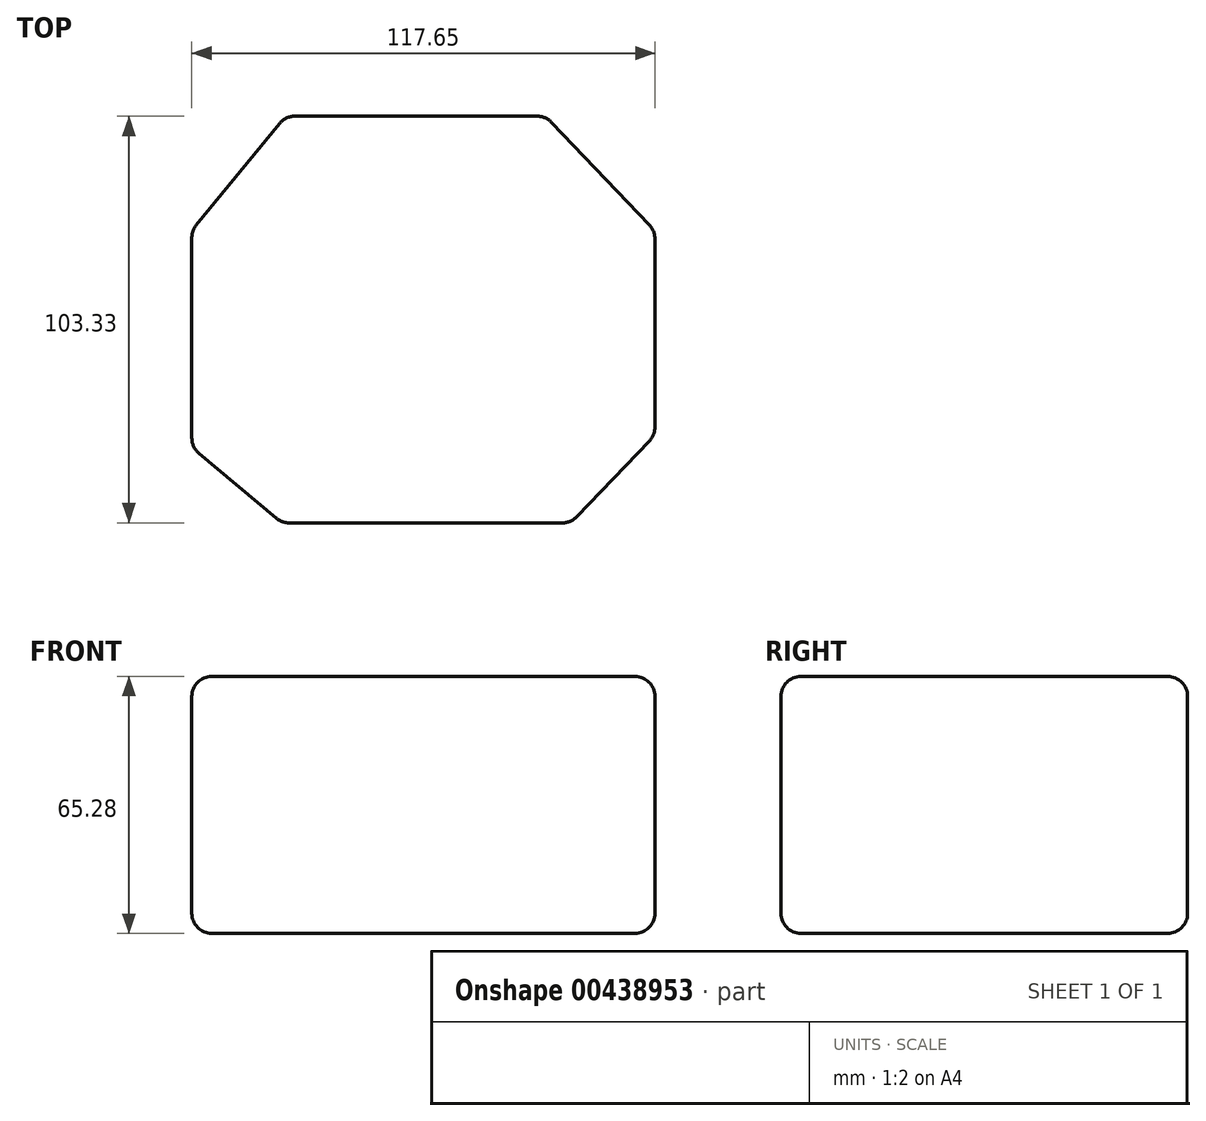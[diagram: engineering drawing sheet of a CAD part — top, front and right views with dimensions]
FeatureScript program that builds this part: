
annotation { "Feature Type Name" : "Feature", "Feature Type Description" : "" }
export const myFeature = defineFeature(function(context is Context, id is Id, definition is map)
    precondition{}
    {
        {
            var Q0;
            Q0=qCreatedBy(makeId("Top.planeOp"),FACE);
            var sketch = newSketch(context, id + "F0", { "sketchPlane" : qUnion([Q0])});
            skLineSegment(sketch, "E0", {"start": v(-32.92, 29.1) * mm, "end": v(33.22, 29.1) * mm});
            skLineSegment(sketch, "E1", {"start": v(33.22, 29.1) * mm, "end": v(60.96, 0) * mm});
            skLineSegment(sketch, "E2", {"start": v(60.96, 0) * mm, "end": v(60.96, -51.97) * mm});
            skLineSegment(sketch, "E3", {"start": v(60.96, -51.97) * mm, "end": v(39.62, -74.22) * mm});
            skLineSegment(sketch, "E4", {"start": v(39.62, -74.22) * mm, "end": v(-33.83, -74.22) * mm});
            skLineSegment(sketch, "E5", {"start": v(-33.83, -74.22) * mm, "end": v(-56.7, -55.02) * mm});
            skLineSegment(sketch, "E6", {"start": v(-56.7, -55.02) * mm, "end": v(-56.7, 0) * mm});
            skLineSegment(sketch, "E7", {"start": v(-56.7, 0) * mm, "end": v(-32.92, 29.1) * mm});
            skSolve(sketch);
        }
        {
            var Q0;
            Q0 = qSketchRegion(id + "F0", true);
            extrude(context, id + "F1", {"entities" : qUnion([Q0]), "depth" : 65.28 * mm});
        }
        {
            var Q0;
            Q0=makeQuery(id+"F1.opExtrude","SWEPT_FACE",FACE,{"disambiguationData":[OSD([sQuery(id+"F0.wireOp",EDGE,"E0")])]});
            var Q1;
            Q1=makeQuery(id+"F1.opExtrude","SWEPT_FACE",FACE,{"disambiguationData":[OSD([sQuery(id+"F0.wireOp",EDGE,"E1")])]});
            var Q2;
            Q2=makeQuery(id+"F1.opExtrude","SWEPT_FACE",FACE,{"disambiguationData":[OSD([sQuery(id+"F0.wireOp",EDGE,"E7")])]});
            var Q3;
            Q3=makeQuery(id+"F1.opExtrude","SWEPT_FACE",FACE,{"disambiguationData":[OSD([sQuery(id+"F0.wireOp",EDGE,"E6")])]});
            var Q4;
            Q4=makeQuery(id+"F1.opExtrude","SWEPT_FACE",FACE,{"disambiguationData":[OSD([sQuery(id+"F0.wireOp",EDGE,"E5")])]});
            var Q5;
            Q5=makeQuery(id+"F1.opExtrude","SWEPT_FACE",FACE,{"disambiguationData":[OSD([sQuery(id+"F0.wireOp",EDGE,"E4")])]});
            var Q6;
            Q6=makeQuery(id+"F1.opExtrude","SWEPT_FACE",FACE,{"disambiguationData":[OSD([sQuery(id+"F0.wireOp",EDGE,"E3")])]});
            var Q7;
            Q7=makeQuery(id+"F1.opExtrude","SWEPT_FACE",FACE,{"disambiguationData":[OSD([sQuery(id+"F0.wireOp",EDGE,"E2")])]});
            var Q8;
            Q8=makeQuery(id+"F1.opExtrude","CAP_EDGE",EDGE,{"disambiguationData":[OSD([sQuery(id+"F0.wireOp",EDGE,"E7")])],"isStart":false});
            var Q9;
            Q9=makeQuery(id+"F1.opExtrude","CAP_EDGE",EDGE,{"disambiguationData":[OSD([sQuery(id+"F0.wireOp",EDGE,"E3")])],"isStart":false});
            var Q10;
            Q10=makeQuery(id+"F1.opExtrude","CAP_EDGE",EDGE,{"disambiguationData":[OSD([sQuery(id+"F0.wireOp",EDGE,"E5")])],"isStart":false});
            var Q11;
            Q11=makeQuery(id+"F1.opExtrude","CAP_EDGE",EDGE,{"disambiguationData":[OSD([sQuery(id+"F0.wireOp",EDGE,"E5")])],"isStart":true});
            var Q12;
            Q12=makeQuery(id+"F1.opExtrude","CAP_EDGE",EDGE,{"disambiguationData":[OSD([sQuery(id+"F0.wireOp",EDGE,"E1")])],"isStart":false});
            var Q13;
            Q13=makeQuery(id+"F1.opExtrude","CAP_EDGE",EDGE,{"disambiguationData":[OSD([sQuery(id+"F0.wireOp",EDGE,"E7")])],"isStart":true});
            var Q14;
            Q14=makeQuery(id+"F1.opExtrude","CAP_EDGE",EDGE,{"disambiguationData":[OSD([sQuery(id+"F0.wireOp",EDGE,"E3")])],"isStart":true});
            var Q15;
            Q15=makeQuery(id+"F1.opExtrude","CAP_EDGE",EDGE,{"disambiguationData":[OSD([sQuery(id+"F0.wireOp",EDGE,"E6")])],"isStart":false});
            var Q16;
            Q16=makeQuery(id+"F1.opExtrude","CAP_EDGE",EDGE,{"disambiguationData":[OSD([sQuery(id+"F0.wireOp",EDGE,"E6")])],"isStart":true});
            var Q17;
            Q17=makeQuery(id+"F1.opExtrude","SWEPT_EDGE",EDGE,{"disambiguationData":[OSD([sQuery(id+"F0.wireOp",EDGE,"E5"),sQuery(id+"F0.wireOp",EDGE,"E6")])]});
            var Q18;
            Q18=makeQuery(id+"F1.opExtrude","CAP_EDGE",EDGE,{"disambiguationData":[OSD([sQuery(id+"F0.wireOp",EDGE,"E0")])],"isStart":false});
            var Q19;
            Q19=makeQuery(id+"F1.opExtrude","SWEPT_EDGE",EDGE,{"disambiguationData":[OSD([sQuery(id+"F0.wireOp",EDGE,"E6"),sQuery(id+"F0.wireOp",EDGE,"E7")])]});
            var Q20;
            Q20=makeQuery(id+"F1.opExtrude","SWEPT_EDGE",EDGE,{"disambiguationData":[OSD([sQuery(id+"F0.wireOp",EDGE,"E0"),sQuery(id+"F0.wireOp",EDGE,"E1")])]});
            var Q21;
            Q21=makeQuery(id+"F1.opExtrude","SWEPT_EDGE",EDGE,{"disambiguationData":[OSD([sQuery(id+"F0.wireOp",EDGE,"E0"),sQuery(id+"F0.wireOp",EDGE,"E7")])]});
            var Q22;
            Q22=makeQuery(id+"F1.opExtrude","CAP_EDGE",EDGE,{"disambiguationData":[OSD([sQuery(id+"F0.wireOp",EDGE,"E1")])],"isStart":true});
            var Q23;
            Q23=makeQuery(id+"F1.opExtrude","CAP_EDGE",EDGE,{"disambiguationData":[OSD([sQuery(id+"F0.wireOp",EDGE,"E2")])],"isStart":true});
            var Q24;
            Q24=makeQuery(id+"F1.opExtrude","SWEPT_EDGE",EDGE,{"disambiguationData":[OSD([sQuery(id+"F0.wireOp",EDGE,"E1"),sQuery(id+"F0.wireOp",EDGE,"E2")])]});
            var Q25;
            Q25=makeQuery(id+"F1.opExtrude","SWEPT_EDGE",EDGE,{"disambiguationData":[OSD([sQuery(id+"F0.wireOp",EDGE,"E4"),sQuery(id+"F0.wireOp",EDGE,"E5")])]});
            var Q26;
            Q26=makeQuery(id+"F1.opExtrude","SWEPT_EDGE",EDGE,{"disambiguationData":[OSD([sQuery(id+"F0.wireOp",EDGE,"E2"),sQuery(id+"F0.wireOp",EDGE,"E3")])]});
            var Q27;
            Q27=makeQuery(id+"F1.opExtrude","CAP_EDGE",EDGE,{"disambiguationData":[OSD([sQuery(id+"F0.wireOp",EDGE,"E2")])],"isStart":false});
            var Q28;
            Q28=makeQuery(id+"F1.opExtrude","CAP_EDGE",EDGE,{"disambiguationData":[OSD([sQuery(id+"F0.wireOp",EDGE,"E4")])],"isStart":true});
            var Q29;
            Q29=makeQuery(id+"F1.opExtrude","CAP_EDGE",EDGE,{"disambiguationData":[OSD([sQuery(id+"F0.wireOp",EDGE,"E0")])],"isStart":true});
            var Q30;
            Q30=makeQuery(id+"F1.opExtrude","SWEPT_EDGE",EDGE,{"disambiguationData":[OSD([sQuery(id+"F0.wireOp",EDGE,"E3"),sQuery(id+"F0.wireOp",EDGE,"E4")])]});
            var Q31;
            Q31=makeQuery(id+"F1.opExtrude","CAP_EDGE",EDGE,{"disambiguationData":[OSD([sQuery(id+"F0.wireOp",EDGE,"E4")])],"isStart":false});
            var Q32;
            Q32=makeQuery(id+"F1.opExtrude","CAP_FACE",FACE,{"disambiguationData":[OSD([sQuery(id+"F0.wireOp",EDGE,"E0"),sQuery(id+"F0.wireOp",EDGE,"E1"),sQuery(id+"F0.wireOp",EDGE,"E2"),sQuery(id+"F0.wireOp",EDGE,"E3"),sQuery(id+"F0.wireOp",EDGE,"E4"),sQuery(id+"F0.wireOp",EDGE,"E5"),sQuery(id+"F0.wireOp",EDGE,"E6"),sQuery(id+"F0.wireOp",EDGE,"E7")])],"isStart":false});
            fillet(context, id + "F2", {"entities" : qUnion([Q0, Q1, Q2, Q3, Q4, Q5, Q6, Q7, Q8, Q9, Q10, Q11, Q12, Q13, Q14, Q15, Q16, Q17, Q18, Q19, Q20, Q21, Q22, Q23, Q24, Q25, Q26, Q27, Q28, Q29, Q30, Q31, Q32]), "radius" : 5.08 * mm, "tangentPropagation" : true, "allowEdgeOverflow" : false});
        }
    });
